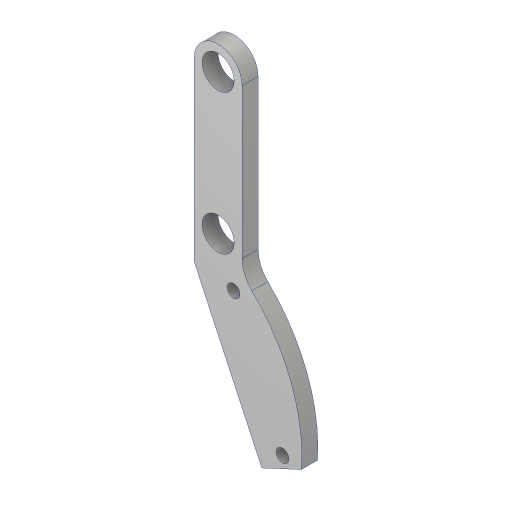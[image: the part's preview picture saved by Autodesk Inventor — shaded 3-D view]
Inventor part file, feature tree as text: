
AUTODESK INVENTOR PART (.ipt)
format: ipt  version: 2023.2 (Build 272271000, 271)  size: 172,544 bytes
history: native  units: mm
features: extrude x4, sketch x4, fillet x2, other x1, projected_geometry x1
ambient origin geometry x8: Origin, YZ Plane, XZ Plane, XY Plane, X Axis, Y Axis, Z Axis, Center Point
bodies: Body1 (feature_tree)
feature tree (12):
  other  "솔리드1"
  extrude  "돌출1"  Depth=20.0mm
  fillet  "모깎기1"  Radius=11.34464mm
  extrude  "돌출2"  Depth=7.0mm
  extrude  "돌출4"  TaperAngle=90.0deg  [1 undecoded]
  extrude  "돌출6"  Depth=20.0mm
  fillet  "모깎기3"  Radius=11.34464mm
  sketch  "스케치1"
  sketch  "스케치2"
  sketch  "스케치4"
  sketch  "스케치6"
  projected_geometry  "투영된 루프1"
note: 1 required parameter value undecoded (feature->parameter linkage not recoverable at this tier; creation-order binding heuristic only, values carry confidence <= 0.55)
